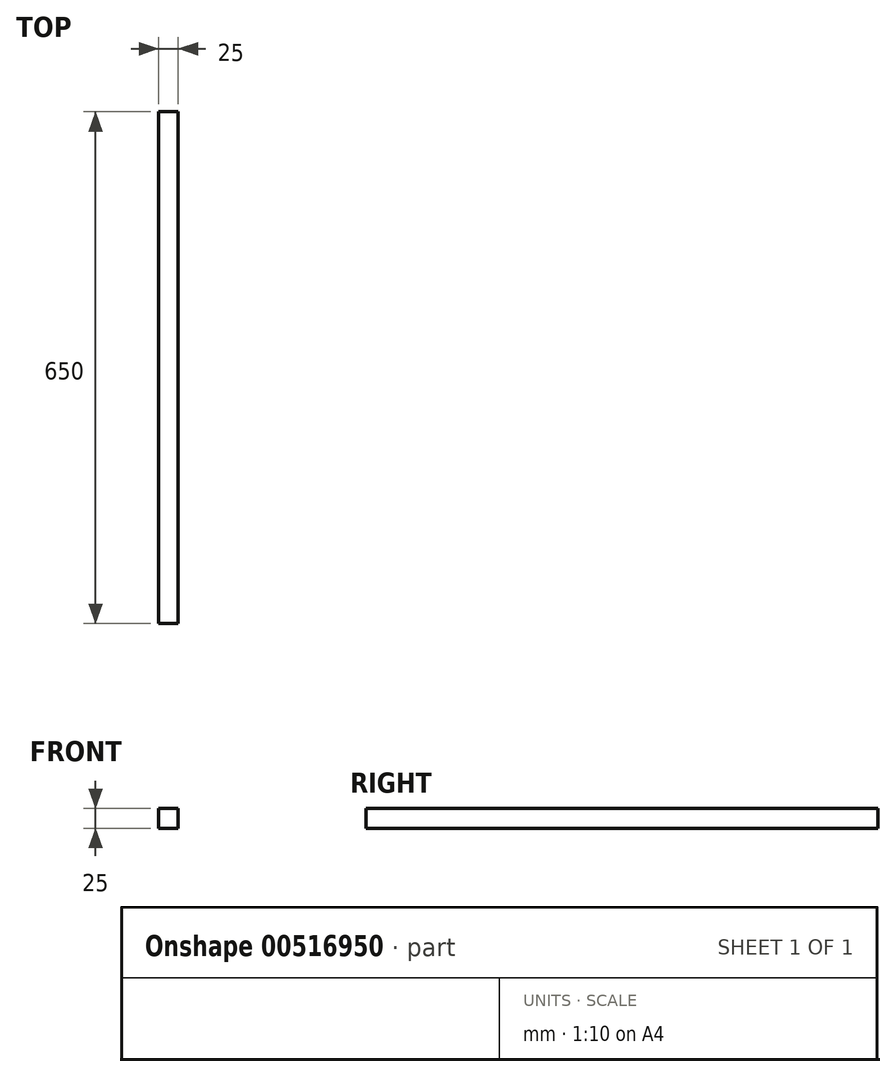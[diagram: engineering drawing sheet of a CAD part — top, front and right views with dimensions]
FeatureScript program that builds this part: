
annotation { "Feature Type Name" : "Feature", "Feature Type Description" : "" }
export const myFeature = defineFeature(function(context is Context, id is Id, definition is map)
    precondition{}
    {
        {
            var Q0;
            Q0=qCreatedBy(makeId("Front.planeOp"),FACE);
            var sketch = newSketch(context, id + "F0", { "sketchPlane" : qUnion([Q0])});
            skLineSegment(sketch, "E0.bottom", {"start": v(-73.64, 50.42) * mm, "end": v(-48.64, 50.42) * mm});
            skLineSegment(sketch, "E0.top", {"start": v(-73.64, 25.42) * mm, "end": v(-48.64, 25.42) * mm});
            skLineSegment(sketch, "E0.left", {"start": v(-73.64, 50.42) * mm, "end": v(-73.64, 25.42) * mm});
            skLineSegment(sketch, "E0.right", {"start": v(-48.64, 50.42) * mm, "end": v(-48.64, 25.42) * mm});
            skSolve(sketch);
        }
        {
            var Q0;
            Q0=makeQuery(id+"F0.imprint","IMPRINT",FACE,{"disambiguationData":[TD([[makeQuery(id+"F0.imprint","IMPRINT",EDGE,{"derivedFrom":sQuery(id+"F0.wireOp",EDGE,"E0.bottom")}),-1.0]])]});
            extrude(context, id + "F1", {"entities" : qUnion([Q0]), "depth" : 650 * mm, "offsetDistance" : 25 * mm});
        }
    });
